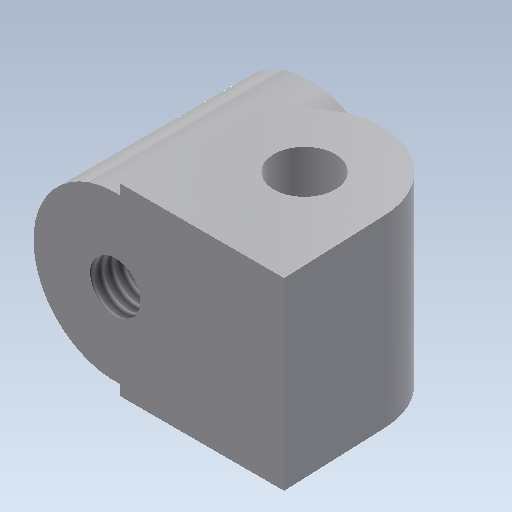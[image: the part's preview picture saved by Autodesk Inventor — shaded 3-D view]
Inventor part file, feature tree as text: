
AUTODESK INVENTOR PART (.ipt)
format: ipt  version: 2020 (Build 240168000, 168)  size: 125,440 bytes
history: native  units: mm
features: extrude x2, hole x2, sketch x2
ambient origin geometry x8: Origin, YZ Plane, XZ Plane, XY Plane, X Axis, Y Axis, Z Axis, Center Point
bodies: Solid1 (feature_tree)
feature tree (6):
  extrude  "Extrusion1"  Depth=5.0mm
  extrude  "Extrusion2"  Depth=4.0mm TaperAngle=0.0deg
  hole  "Hole1"  [1 undecoded]
  hole  "Hole2"  [1 undecoded]
  sketch  "Sketch1"  dims[d0=3.8mm d1=5.0mm]
  sketch  "Sketch2"  dims[d2=8.0mm d3=9.0mm d4=0.0mm d5=8.0mm d6=4.25mm d7=9.5mm d8=0.0mm d9=10.0mm d10=10.0mm d11=3.0mm d12=6.0mm d13=4.0mm d14=2.0mm d15=90.0deg d16=6.0mm d17=0.0mm d18=10.0mm d19=10.0mm d20=2.459mm d21=6.0mm d22=4.0mm d23=2.0mm d24=90.0deg d25=12.05mm d26=0.0mm]
note: 2 required parameter values undecoded (feature->parameter linkage not recoverable at this tier; creation-order binding heuristic only, values carry confidence <= 0.55)
